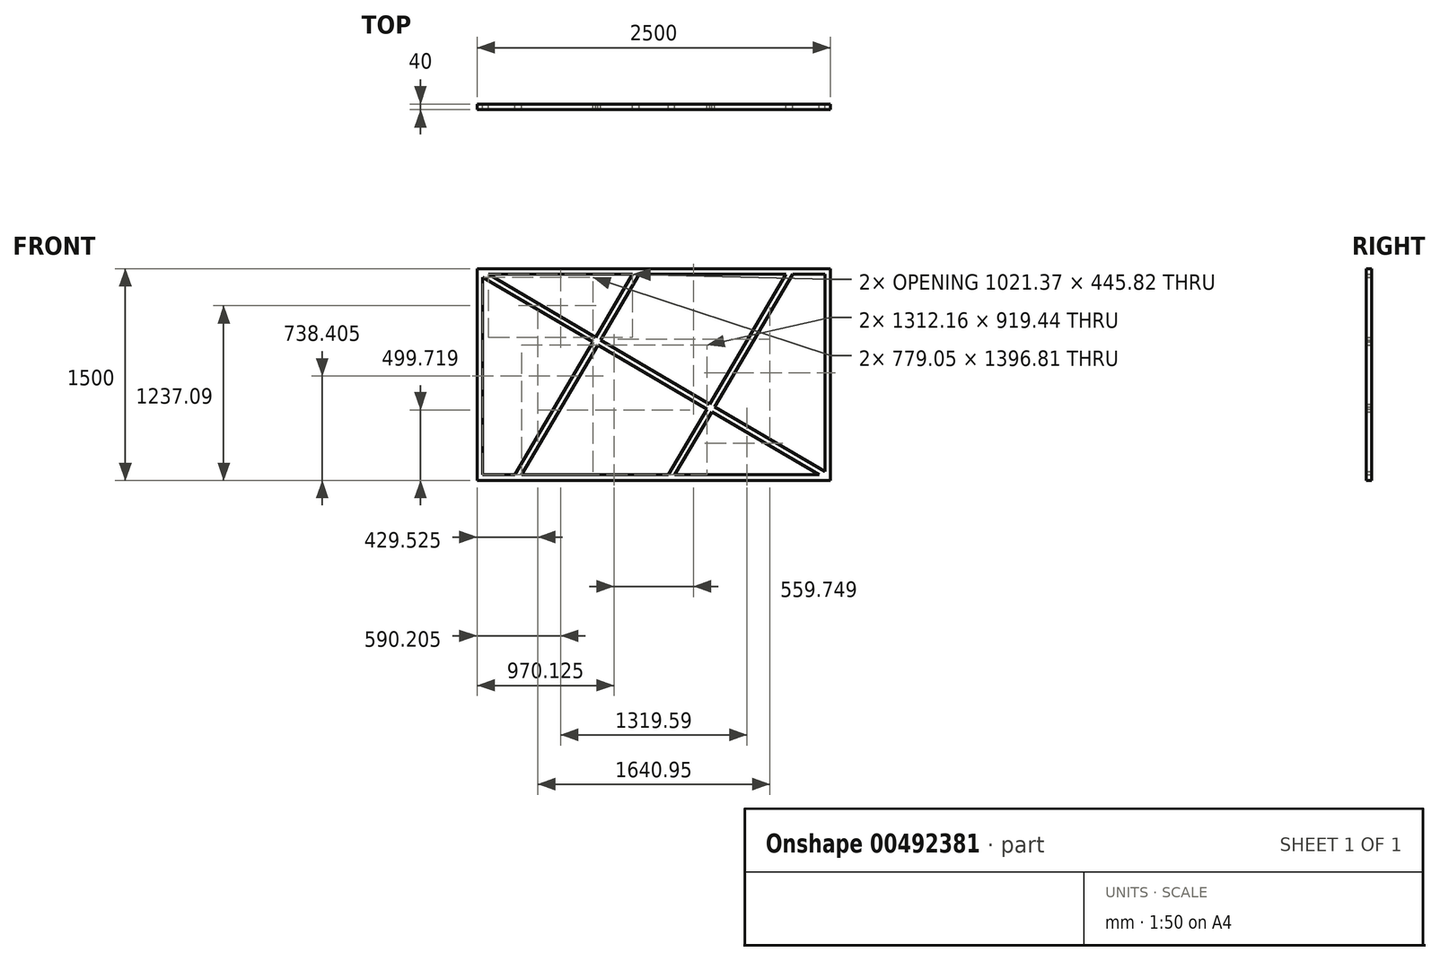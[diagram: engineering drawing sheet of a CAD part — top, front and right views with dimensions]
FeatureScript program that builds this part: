
annotation { "Feature Type Name" : "Feature", "Feature Type Description" : "" }
export const myFeature = defineFeature(function(context is Context, id is Id, definition is map)
    precondition{}
    {
        {
            var Q0;
            Q0=qCreatedBy(makeId("Front.planeOp"),FACE);
            var sketch = newSketch(context, id + "F0", { "sketchPlane" : qUnion([Q0])});
            skLineSegment(sketch, "E0.bottom", {"start": v(0, 0) * mm, "end": v(2500, 0) * mm});
            skLineSegment(sketch, "E0.top", {"start": v(0, 1500) * mm, "end": v(2500, 1500) * mm});
            skLineSegment(sketch, "E0.left", {"start": v(0, 0) * mm, "end": v(0, 1500) * mm});
            skLineSegment(sketch, "E0.right", {"start": v(2500, 0) * mm, "end": v(2500, 1500) * mm});
            skLineSegment(sketch, "E1.0", {"start": v(40, 1460) * mm, "end": v(2460, 1460) * mm});
            skLineSegment(sketch, "E1.1", {"start": v(40, 40) * mm, "end": v(40, 1460) * mm});
            skLineSegment(sketch, "E1.2", {"start": v(40, 40) * mm, "end": v(2460, 40) * mm});
            skLineSegment(sketch, "E1.3", {"start": v(2460, 40) * mm, "end": v(2460, 1460) * mm});
            skLineSegment(sketch, "E2", {"start": v(40, 1460) * mm, "end": v(2460, 40) * mm, "construction": true});
            skLineSegment(sketch, "E3.0", {"start": v(40, 1436.81) * mm, "end": v(2420.48, 40) * mm});
            skLineSegment(sketch, "E4.0", {"start": v(79.52, 1460) * mm, "end": v(2460, 63.19) * mm});
            skLineSegment(sketch, "E5", {"start": v(290.86, 40) * mm, "end": v(1124.08, 1460) * mm, "construction": true});
            skLineSegment(sketch, "E6", {"start": v(1375.92, 40) * mm, "end": v(2209.14, 1460) * mm, "construction": true});
            skLineSegment(sketch, "E7.0", {"start": v(314.04, 40) * mm, "end": v(1147.27, 1460) * mm});
            skLineSegment(sketch, "E8.0", {"start": v(267.67, 40) * mm, "end": v(1100.89, 1460) * mm});
            skLineSegment(sketch, "E9.0", {"start": v(1399.11, 40) * mm, "end": v(2232.33, 1460) * mm});
            skLineSegment(sketch, "E10.0", {"start": v(1352.73, 40) * mm, "end": v(2185.96, 1460) * mm});
            skSolve(sketch);
        }
        {
            var Q0;
            Q0 = qSketchRegion(id + "F0", true);
            var Q1;
            {var subQ0=sQuery(id+"F0.wireOp",EDGE,"E7.0");var subQ1=sQuery(id+"F0.wireOp",EDGE,"E1.2");var subQ2=makeQuery(id+"F0.imprint","INTERSECT",VERTEX,{"derivedFrom":[subQ1,subQ0]});Q1=makeQuery(id+"F0.imprint","IMPRINT",FACE,{"disambiguationData":[TD([[makeQuery(id+"F0.imprint","IMPRINT",EDGE,{"disambiguationData":[TD([[subQ2,1.0]])],"derivedFrom":subQ1}),1.0]])]});}
            var Q2;
            {var subQ1=sQuery(id+"F0.wireOp",EDGE,"E1.0");var subQ6=sQuery(id+"F0.wireOp",EDGE,"E1.1");var subQ9=makeQuery(id+"F0.imprint","INTERSECT",VERTEX,{"derivedFrom":[subQ1,subQ6]});Q2=makeQuery(id+"F0.imprint","IMPRINT",FACE,{"disambiguationData":[TD([[makeQuery(id+"F0.imprint","IMPRINT",EDGE,{"disambiguationData":[TD([[subQ9,-1.0]])],"derivedFrom":subQ1}),-1.0]])]});}
            var Q3;
            {var subQ0=sQuery(id+"F0.wireOp",EDGE,"E8.0");var subQ1=sQuery(id+"F0.wireOp",EDGE,"E3.0");var subQ2=makeQuery(id+"F0.imprint","INTERSECT",VERTEX,{"derivedFrom":[subQ1,subQ0]});Q3=makeQuery(id+"F0.imprint","IMPRINT",FACE,{"disambiguationData":[TD([[makeQuery(id+"F0.imprint","IMPRINT",EDGE,{"disambiguationData":[TD([[subQ2,-1.0]])],"derivedFrom":subQ1}),1.0]])]});}
            var Q4;
            {var subQ0=sQuery(id+"F0.wireOp",EDGE,"E7.0");var subQ1=sQuery(id+"F0.wireOp",EDGE,"E1.0");var subQ2=makeQuery(id+"F0.imprint","INTERSECT",VERTEX,{"derivedFrom":[subQ1,subQ0]});Q4=makeQuery(id+"F0.imprint","IMPRINT",FACE,{"disambiguationData":[TD([[makeQuery(id+"F0.imprint","IMPRINT",EDGE,{"disambiguationData":[TD([[subQ2,1.0]])],"derivedFrom":subQ1}),-1.0]])]});}
            var Q5;
            {var subQ0=sQuery(id+"F0.wireOp",EDGE,"E7.0");var subQ1=sQuery(id+"F0.wireOp",EDGE,"E3.0");var subQ2=makeQuery(id+"F0.imprint","INTERSECT",VERTEX,{"derivedFrom":[subQ1,subQ0]});Q5=makeQuery(id+"F0.imprint","IMPRINT",FACE,{"disambiguationData":[TD([[makeQuery(id+"F0.imprint","IMPRINT",EDGE,{"disambiguationData":[TD([[subQ2,-1.0]])],"derivedFrom":subQ1}),1.0]])]});}
            var Q6;
            {var subQ0=sQuery(id+"F0.wireOp",EDGE,"E9.0");var subQ1=sQuery(id+"F0.wireOp",EDGE,"E1.0");var subQ2=makeQuery(id+"F0.imprint","INTERSECT",VERTEX,{"derivedFrom":[subQ1,subQ0]});Q6=makeQuery(id+"F0.imprint","IMPRINT",FACE,{"disambiguationData":[TD([[makeQuery(id+"F0.imprint","IMPRINT",EDGE,{"disambiguationData":[TD([[subQ2,1.0]])],"derivedFrom":subQ1}),-1.0]])]});}
            var Q7;
            {var subQ1=sQuery(id+"F0.wireOp",EDGE,"E1.3");var subQ5=sQuery(id+"F0.wireOp",EDGE,"E1.2");var subQ6=makeQuery(id+"F0.imprint","INTERSECT",VERTEX,{"derivedFrom":[subQ5,subQ1]});Q7=makeQuery(id+"F0.imprint","IMPRINT",FACE,{"disambiguationData":[TD([[makeQuery(id+"F0.imprint","IMPRINT",EDGE,{"disambiguationData":[TD([[subQ6,1.0]])],"derivedFrom":subQ5}),1.0]])]});}
            var Q8;
            {var subQ0=sQuery(id+"F0.wireOp",EDGE,"E10.0");var subQ1=sQuery(id+"F0.wireOp",EDGE,"E3.0");var subQ2=makeQuery(id+"F0.imprint","INTERSECT",VERTEX,{"derivedFrom":[subQ1,subQ0]});Q8=makeQuery(id+"F0.imprint","IMPRINT",FACE,{"disambiguationData":[TD([[makeQuery(id+"F0.imprint","IMPRINT",EDGE,{"disambiguationData":[TD([[subQ2,-1.0]])],"derivedFrom":subQ1}),1.0]])]});}
            var Q9;
            {var subQ0=sQuery(id+"F0.wireOp",EDGE,"E9.0");var subQ1=sQuery(id+"F0.wireOp",EDGE,"E1.2");var subQ2=makeQuery(id+"F0.imprint","INTERSECT",VERTEX,{"derivedFrom":[subQ1,subQ0]});Q9=makeQuery(id+"F0.imprint","IMPRINT",FACE,{"disambiguationData":[TD([[makeQuery(id+"F0.imprint","IMPRINT",EDGE,{"disambiguationData":[TD([[subQ2,1.0]])],"derivedFrom":subQ1}),1.0]])]});}
            extrude(context, id + "F1", {"entities" : qUnion([Q0, Q1, Q2, Q3, Q4, Q5, Q6, Q7, Q8, Q9]), "depth" : 40 * mm});
        }
    });
